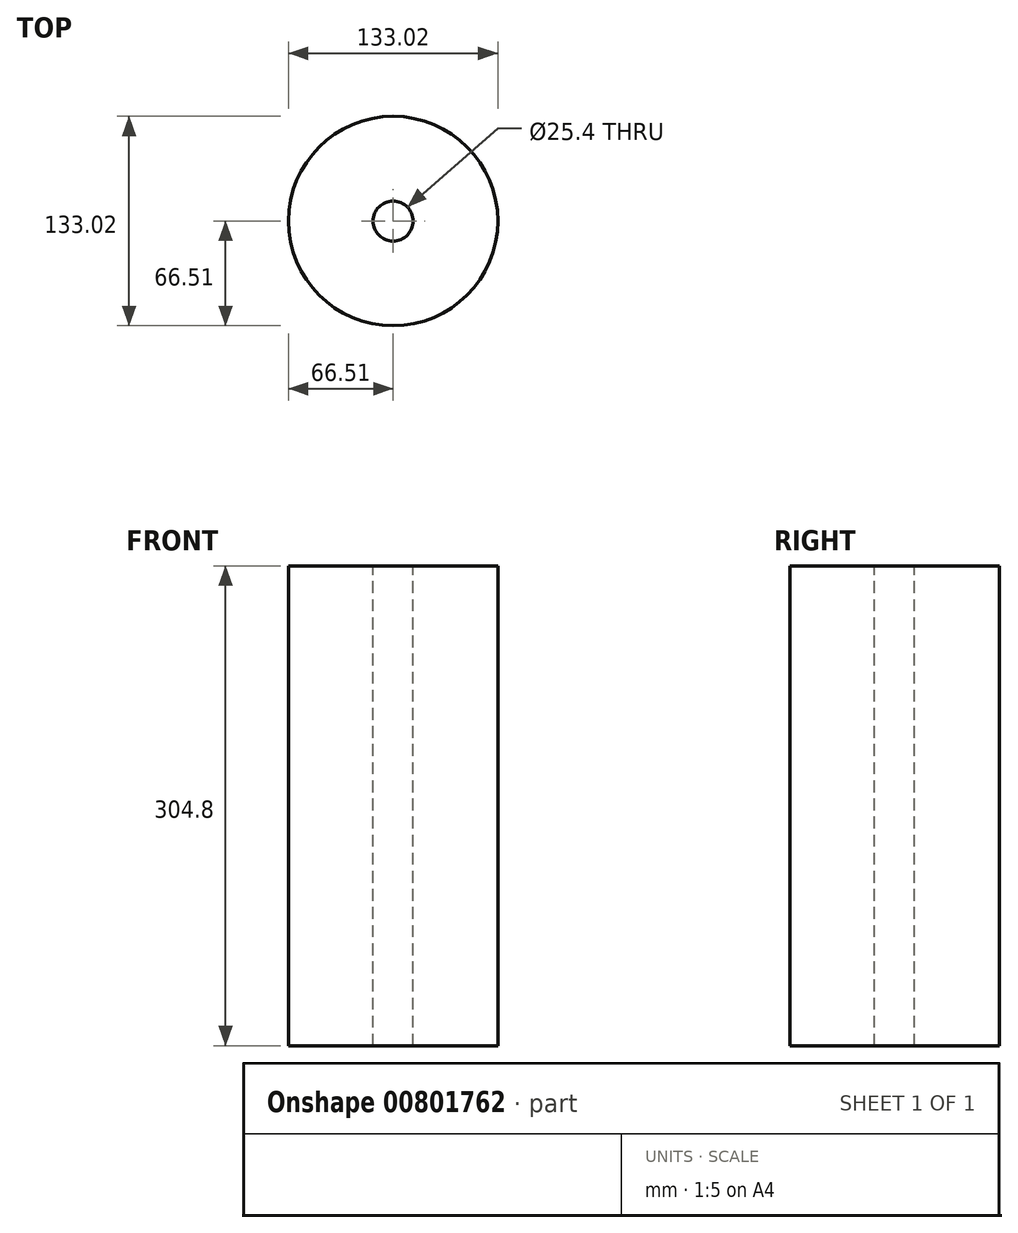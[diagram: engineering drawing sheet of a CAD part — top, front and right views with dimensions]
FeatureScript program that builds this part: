
annotation { "Feature Type Name" : "Feature", "Feature Type Description" : "" }
export const myFeature = defineFeature(function(context is Context, id is Id, definition is map)
    precondition{}
    {
        {
            var Q0;
            Q0=qCreatedBy(makeId("Top.planeOp"),FACE);
            var sketch = newSketch(context, id + "F0", { "sketchPlane" : qUnion([Q0])});
            skCircle(sketch, "E0", {"center": v(0, 0) * mm, "radius": 66.5 * mm});
            skSolve(sketch);
        }
        {
            var Q0;
            Q0=makeQuery(id+"F0.imprint","IMPRINT",FACE,{"disambiguationData":[TD([[makeQuery(id+"F0.imprint","IMPRINT",EDGE,{"derivedFrom":sQuery(id+"F0.wireOp",EDGE,"E0")}),1.0]])]});
            extrude(context, id + "F1", {"entities" : qUnion([Q0]), "oppositeDirection" : true, "depth" : 304.8 * mm, "offsetDistance" : 25.4 * mm});
        }
        {
            var Q0;
            Q0=sQuery(id+"F0.wireOp",VERTEX,"E0.center");
            var Q1;
            Q1=makeQuery(id+"F1.opExtrude","SWEPT_BODY",BODY,{"disambiguationData":[OSD([sQuery(id+"F0.wireOp",EDGE,"E0")])]});
            hole(context, id + "F2", {"style" : HoleStyle.SIMPLE, "endStyle" : HoleEndStyle.THROUGH, "holeDiameter" : 25.4 * mm, "majorDiameter" : 6.35 * mm, "isTappedThrough" : true, "tappedDepth" : 12.7 * mm, "tapClearance" : 3, "locations" : qUnion([Q0]), "scope" : qUnion([Q1])});
        }
    });
